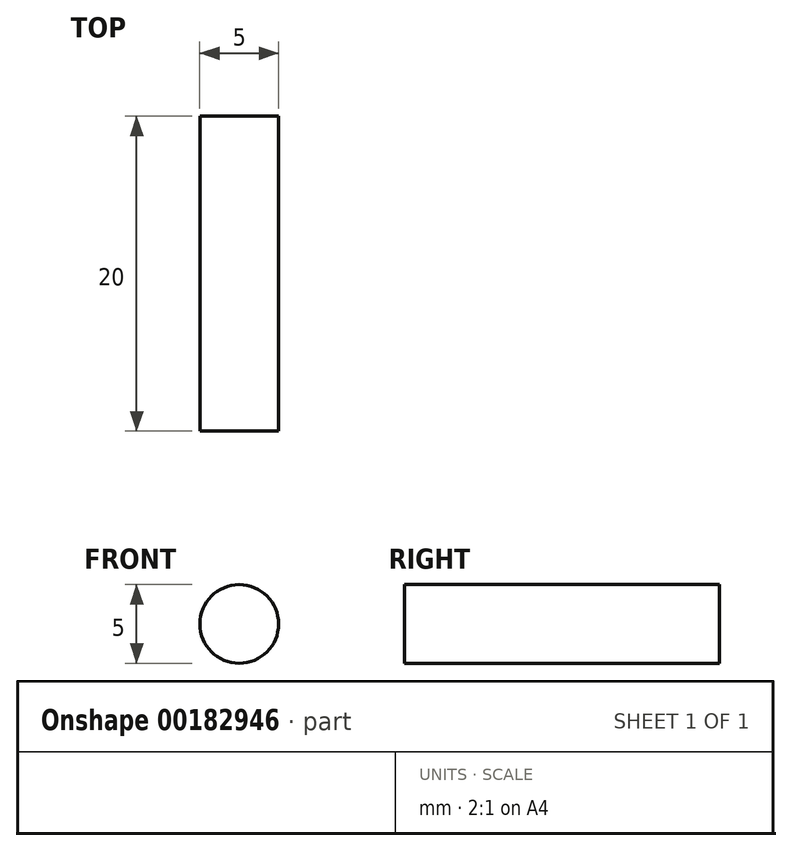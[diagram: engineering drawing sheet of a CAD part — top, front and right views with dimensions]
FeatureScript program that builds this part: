
annotation { "Feature Type Name" : "Feature", "Feature Type Description" : "" }
export const myFeature = defineFeature(function(context is Context, id is Id, definition is map)
    precondition{}
    {
        {
            var Q0;
            Q0=qCreatedBy(makeId("Front.planeOp"),FACE);
            var sketch = newSketch(context, id + "F0", { "sketchPlane" : qUnion([Q0])});
            skCircle(sketch, "E0", {"center": v(-21.55, 24.77) * mm, "radius": 2.5 * mm});
            skSolve(sketch);
        }
        {
            var Q0;
            Q0=makeQuery(id+"F0.imprint","IMPRINT",FACE,{"disambiguationData":[TD([[makeQuery(id+"F0.imprint","IMPRINT",EDGE,{"derivedFrom":sQuery(id+"F0.wireOp",EDGE,"E0")}),1.0]])]});
            extrude(context, id + "F1", {"entities" : qUnion([Q0]), "depth" : 20 * mm});
        }
    });
